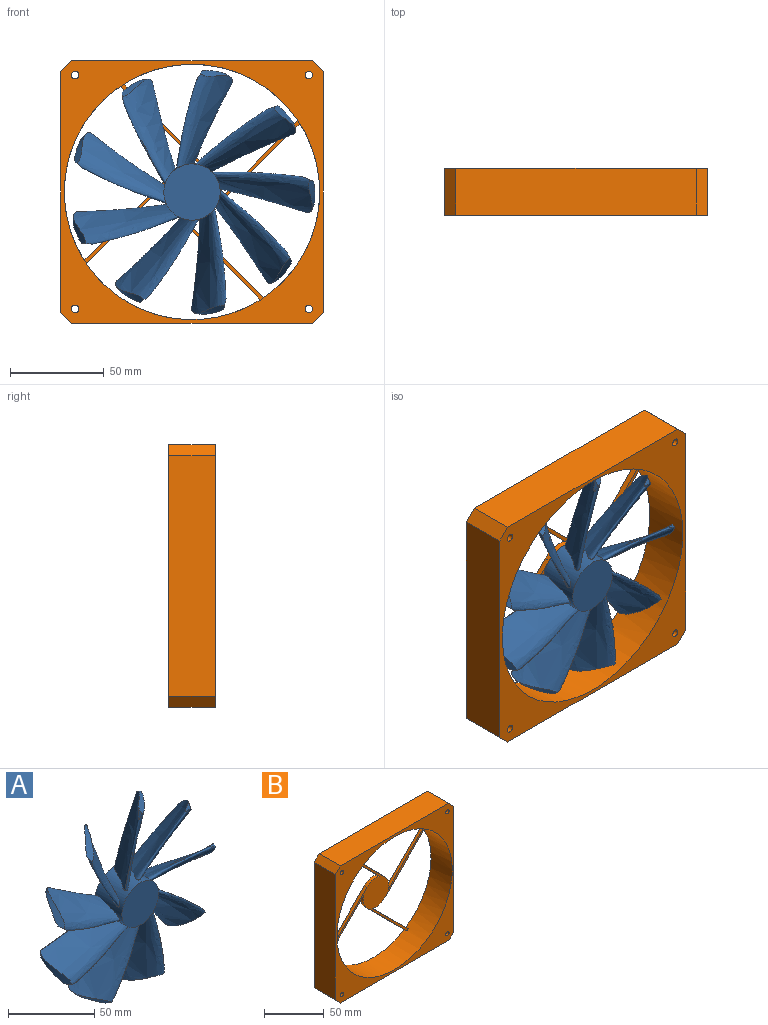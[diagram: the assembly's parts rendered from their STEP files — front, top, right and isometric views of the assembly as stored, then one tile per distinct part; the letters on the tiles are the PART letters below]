
ASSEMBLY  parts=2 mates=1
PART A: 30 faces, bbox 139.2x22.2x138.1 mm
  f0: cylinder r=15mm len=30mm, axis (0,1,0), area 1596.6mm2, adj f1,f2,f3,f6,f9,f12,f15,f18
  f1: plane 30x30mm, normal (0,-1,0), area 706.9mm2, adj f0
  f2: plane 30x30mm, normal (0,1,0), area 706.9mm2, adj f0
  f3: bspline ~56.7x27.16mm, area 2549.1mm2, adj f0,f4,f5
  f4: extruded ~20.74x16.76mm, area 84.8mm2, adj f3,f5
  f5: plane 6x3.72mm, normal (0,0,-1), area 9.6mm2, adj f3,f4
  f6: bspline ~57.25x43.67mm, area 2549.1mm2, adj f0,f7,f8
  f7: extruded ~20.74x17.55mm, area 84.8mm2, adj f6,f8
  f8: plane 4.61x3.88mm, normal (0.64,0,-0.77), area 9.6mm2, adj f6,f7
  f9: bspline ~60.56x21.23mm, area 2549.1mm2, adj f0,f10,f11
  f10: extruded ~20.74x17.78mm, area 84.8mm2, adj f9,f11
  f11: plane 5.91x3.72mm, normal (0.98,0,-0.17), area 9.6mm2, adj f9,f10
  f12: bspline ~57.68x55.46mm, area 2546.2mm2, adj f0,f13,f14
  f13: extruded ~20.74x18.18mm, area 84.8mm2, adj f12,f14
  f14: plane 5.21x3.72mm, normal (0.87,0,0.5), area 9.6mm2, adj f12,f13
  f15: bspline ~62.57x21.23mm, area 2549.1mm2, adj f0,f16,f17
  f16: extruded ~20.74x18.26mm, area 84.8mm2, adj f15,f17
  f17: plane 5.65x3.72mm, normal (0.34,0,0.94), area 9.6mm2, adj f15,f16
  f18: bspline ~53.41x44.92mm, area 2549.1mm2, adj f0,f19,f20
  f19: extruded ~20.74x18.26mm, area 84.8mm2, adj f18,f20
  f20: plane 5.65x3.72mm, normal (-0.34,0,0.94), area 9.6mm2, adj f18,f19
  f21: bspline ~62.69x28.67mm, area 2552.9mm2, adj f0,f22,f23
  f22: extruded ~20.74x18.18mm, area 84.9mm2, adj f21,f23
  f23: plane 5.21x3.72mm, normal (-0.87,0,0.5), area 9.6mm2, adj f21,f22
  f24: bspline ~55.9x36.59mm, area 2549.1mm2, adj f0,f25,f26
  f25: extruded ~20.74x17.78mm, area 84.8mm2, adj f24,f26
  f26: plane 5.91x3.72mm, normal (-0.98,0,-0.17), area 9.6mm2, adj f24,f25
  f27: bspline ~60.9x36.72mm, area 2549.1mm2, adj f0,f28,f29
  f28: extruded ~20.74x17.55mm, area 84.8mm2, adj f27,f29
  f29: plane 4.61x3.88mm, normal (-0.64,0,-0.77), area 9.6mm2, adj f27,f28
PART B: 28 faces, bbox 140x25x140 mm
  f0: plane 115.01x115.01mm, normal (0,-1,0), area 1198.7mm2, adj f4,f5,f6,f7,f8,f9,f10,f11
  f1: plane 128x25mm, normal (-1,0,0), area 3200mm2, adj f22,f23,f24,f27
  f2: plane 128x25mm, normal (0,0,-1), area 3200mm2, adj f22,f23,f26,f27
  f3: plane 128x25mm, normal (1,0,0), area 3200mm2, adj f22,f23,f25,f26
  f4: plane 46.9x46.9mm, normal (0.71,0,-0.71), area 199mm2, adj f0,f5,f17,f22
  f5: cylinder r=68mm len=136mm, axis (0,-1,0), area 10656.9mm2, adj f0,f4,f6,f7,f9,f11,f18,f19
  f6: plane 41.91x41.91mm, normal (0.71,0,0.71), area 177.8mm2, adj f0,f5,f17,f22
  f7: plane 41.91x41.91mm, normal (-0.71,0,0.71), area 177.8mm2, adj f0,f5,f8,f22
  f8: cylinder r=15mm len=14.51mm, axis (0,-1,0), area 47.2mm2, adj f0,f7,f18,f22
  f9: plane 41.91x41.91mm, normal (-0.71,0,-0.71), area 177.8mm2, adj f0,f5,f10,f22
  f10: cylinder r=15mm len=14.51mm, axis (0,-1,0), area 47.2mm2, adj f0,f9,f19,f22
  f11: plane 41.91x41.91mm, normal (0.71,0,-0.71), area 177.8mm2, adj f0,f5,f12,f22
  f12: cylinder r=15mm len=14.51mm, axis (0,-1,0), area 47.2mm2, adj f0,f11,f20,f22
  f13: cylinder r=2mm len=25mm, axis (0,-1,0), area 314.2mm2, adj f22,f23
  f14: cylinder r=2mm len=25mm, axis (0,-1,0), area 314.2mm2, adj f22,f23
  f15: cylinder r=2mm len=25mm, axis (0,-1,0), area 314.2mm2, adj f22,f23
  f16: cylinder r=2mm len=25mm, axis (0,-1,0), area 314.2mm2, adj f22,f23
  f17: cylinder r=15mm len=14.51mm, axis (0,-1,0), area 47.2mm2, adj f0,f4,f6,f22
  f18: plane 46.9x46.9mm, normal (0.71,0,0.71), area 199mm2, adj f0,f5,f8,f22
  f19: plane 46.9x46.9mm, normal (-0.71,0,0.71), area 199mm2, adj f0,f5,f10,f22
  f20: plane 46.9x46.9mm, normal (-0.71,0,-0.71), area 199mm2, adj f0,f5,f12,f22
  f21: plane 128x25mm, normal (0,0,1), area 3200mm2, adj f22,f23,f24,f25
  f22: plane 140x140mm, normal (0,1,0), area 6149.7mm2, adj f1,f2,f3,f4,f5,f6,f7,f8
  f23: plane 140x140mm, normal (0,-1,0), area 4951mm2, adj f1,f2,f3,f5,f13,f14,f15,f16
  f24: plane 25x6mm, normal (-0.71,0,0.71), area 212.1mm2, adj f1,f21,f22,f23
  f25: plane 25x6mm, normal (0.71,0,0.71), area 212.1mm2, adj f3,f21,f22,f23
  f26: plane 25x6mm, normal (0.71,0,-0.71), area 212.1mm2, adj f2,f3,f22,f23
  f27: plane 25x6mm, normal (-0.71,0,-0.71), area 212.1mm2, adj f1,f2,f22,f23
PLACE A rot(axis=(0,-1,0),37.5deg) t=(-67.99,-6.36,-9.68)mm
PLACE B t=(-78.47,-6.36,-12.56)mm fixed
MATE revolute A.f0 <-> B.f5  axis (0,1,0) through (-77.47,-6.36,4.32)mm
